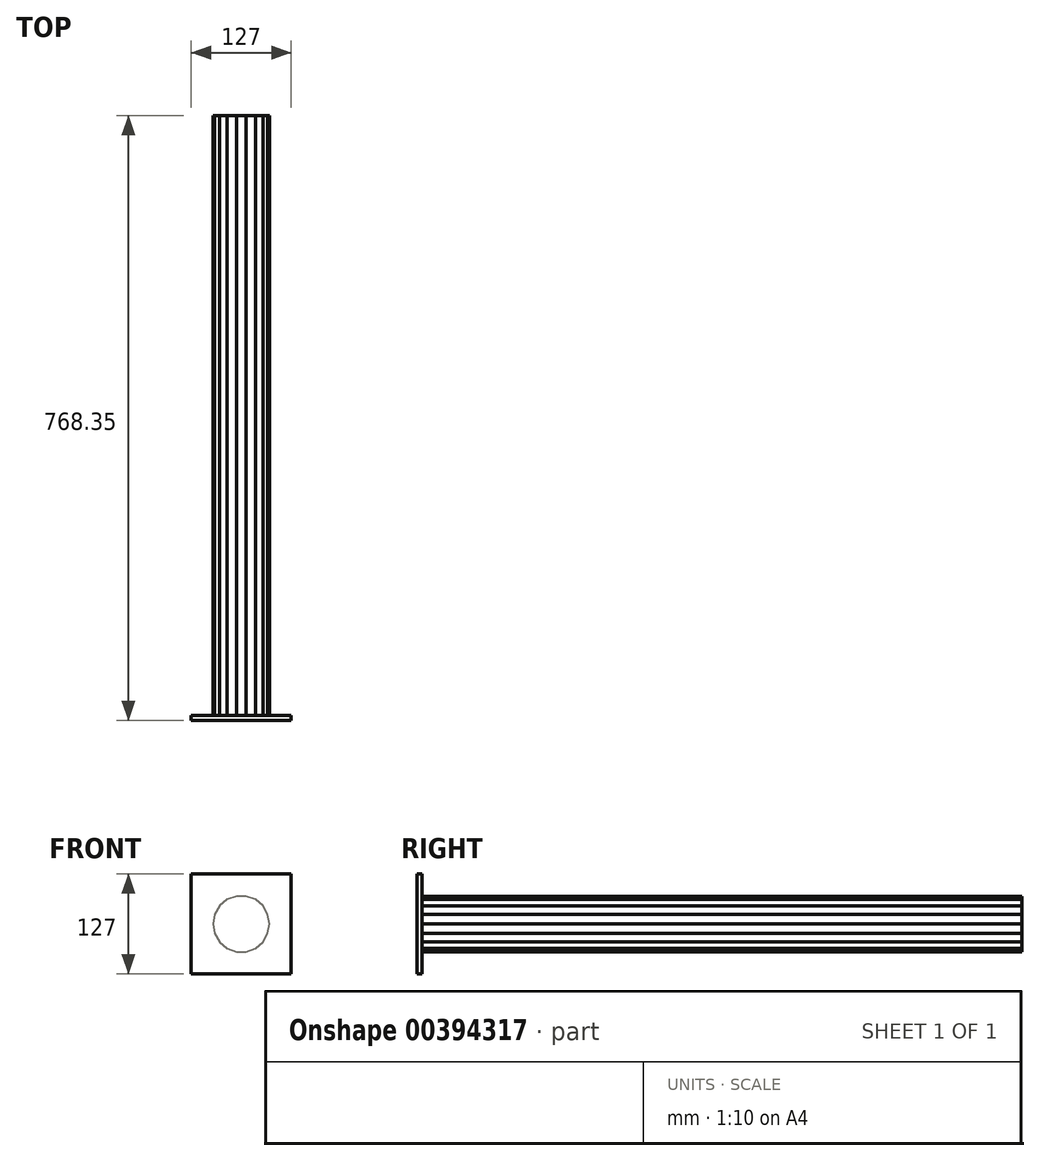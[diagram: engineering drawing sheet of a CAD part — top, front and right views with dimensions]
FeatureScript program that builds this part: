
annotation { "Feature Type Name" : "Feature", "Feature Type Description" : "" }
export const myFeature = defineFeature(function(context is Context, id is Id, definition is map)
    precondition{}
    {
        {
            var Q0;
            Q0=qCreatedBy(makeId("Front.planeOp"),FACE);
            var sketch = newSketch(context, id + "F0", { "sketchPlane" : qUnion([Q0])});
            skLineSegment(sketch, "E0.bottom", {"start": v(-58.32, 61.66) * mm, "end": v(68.68, 61.66) * mm});
            skLineSegment(sketch, "E0.top", {"start": v(-58.32, -65.34) * mm, "end": v(68.68, -65.34) * mm});
            skLineSegment(sketch, "E0.left", {"start": v(-58.32, 61.66) * mm, "end": v(-58.32, -65.34) * mm});
            skLineSegment(sketch, "E0.right", {"start": v(68.68, 61.66) * mm, "end": v(68.68, -65.34) * mm});
            skSolve(sketch);
        }
        {
            var Q0;
            Q0=makeQuery(id+"F0.imprint","IMPRINT",FACE,{"disambiguationData":[TD([[makeQuery(id+"F0.imprint","IMPRINT",EDGE,{"derivedFrom":sQuery(id+"F0.wireOp",EDGE,"E0.bottom")}),-1.0]])]});
            extrude(context, id + "F1", {"entities" : qUnion([Q0]), "depth" : 6.35 * mm});
        }
        {
            var Q0;
            Q0=makeQuery(id+"F1.opExtrude","SWEPT_FACE",FACE,{"disambiguationData":[OSD([sQuery(id+"F0.wireOp",EDGE,"E0.top")])]});
            var sketch = newSketch(context, id + "F2", { "sketchPlane" : qUnion([Q0])});
            skPoint(sketch, "E1", {"position": v(5.18, 69.85) * mm});
            skSolve(sketch);
        }
        {
            var Q0;
            Q0=makeQuery(id+"F1.opExtrude","CAP_FACE",FACE,{"disambiguationData":[OSD([sQuery(id+"F0.wireOp",EDGE,"E0.bottom"),sQuery(id+"F0.wireOp",EDGE,"E0.top"),sQuery(id+"F0.wireOp",EDGE,"E0.left"),sQuery(id+"F0.wireOp",EDGE,"E0.right")])],"isStart":true});
            var sketch = newSketch(context, id + "F3", { "sketchPlane" : qUnion([Q0])});
            skPoint(sketch, "E2", {"position": v(-5.18, -1.84) * mm});
            skCircle(sketch, "E3.cCircle", {"center": v(-5.18, -1.84) * mm, "radius": 35.23 * mm, "construction": true});
            skLineSegment(sketch, "E3.0", {"start": v(1.03, -37.07) * mm, "end": v(-11.4, -37.07) * mm});
            skLineSegment(sketch, "E3.1", {"start": v(-11.4, -37.07) * mm, "end": v(-23.07, -32.82) * mm});
            skLineSegment(sketch, "E3.2", {"start": v(-23.07, -32.82) * mm, "end": v(-32.59, -24.83) * mm});
            skLineSegment(sketch, "E3.3", {"start": v(-32.59, -24.83) * mm, "end": v(-38.8, -14.07) * mm});
            skLineSegment(sketch, "E3.4", {"start": v(-38.8, -14.07) * mm, "end": v(-40.96, -1.84) * mm});
            skLineSegment(sketch, "E3.5", {"start": v(-40.96, -1.84) * mm, "end": v(-38.8, 10.4) * mm});
            skLineSegment(sketch, "E3.6", {"start": v(-38.8, 10.4) * mm, "end": v(-32.59, 21.16) * mm});
            skLineSegment(sketch, "E3.7", {"start": v(-32.59, 21.16) * mm, "end": v(-23.07, 29.15) * mm});
            skLineSegment(sketch, "E3.8", {"start": v(-23.07, 29.15) * mm, "end": v(-11.4, 33.4) * mm});
            skLineSegment(sketch, "E3.9", {"start": v(-11.4, 33.4) * mm, "end": v(1.03, 33.4) * mm});
            skLineSegment(sketch, "E3.10", {"start": v(1.03, 33.4) * mm, "end": v(12.7, 29.15) * mm});
            skLineSegment(sketch, "E3.11", {"start": v(12.7, 29.15) * mm, "end": v(22.23, 21.16) * mm});
            skLineSegment(sketch, "E3.12", {"start": v(22.23, 21.16) * mm, "end": v(28.44, 10.4) * mm});
            skLineSegment(sketch, "E3.13", {"start": v(28.44, 10.4) * mm, "end": v(30.6, -1.84) * mm});
            skLineSegment(sketch, "E3.14", {"start": v(30.6, -1.84) * mm, "end": v(28.44, -14.07) * mm});
            skLineSegment(sketch, "E3.15", {"start": v(28.44, -14.07) * mm, "end": v(22.23, -24.83) * mm});
            skLineSegment(sketch, "E3.16", {"start": v(22.23, -24.83) * mm, "end": v(12.7, -32.82) * mm});
            skLineSegment(sketch, "E3.17", {"start": v(12.7, -32.82) * mm, "end": v(1.03, -37.07) * mm});
            skPoint(sketch, "E3.0.midPoint", {"position": v(-5.18, -37.07) * mm});
            skSolve(sketch);
        }
        {
            var Q0;
            Q0=makeQuery(id+"F3.imprint","IMPRINT",FACE,{"disambiguationData":[TD([[makeQuery(id+"F3.imprint","IMPRINT",EDGE,{"derivedFrom":sQuery(id+"F3.wireOp",EDGE,"E3.0")}),-1.0]])]});
            extrude(context, id + "F4", {"entities" : qUnion([Q0]), "operationType" : NewBodyOperationType.ADD, "depth" : 762 * mm});
        }
    });
